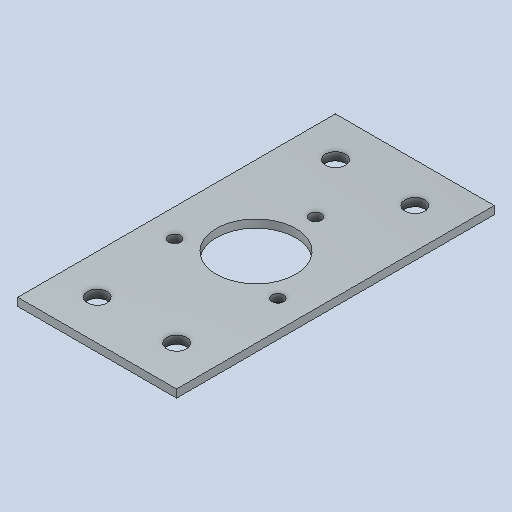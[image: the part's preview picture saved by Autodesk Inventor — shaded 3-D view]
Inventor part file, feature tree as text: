
AUTODESK INVENTOR PART (.ipt)
format: ipt  version: 2023 (Build 270158000, 158)  size: 137,216 bytes
history: native  units: mm
features: other x1, extrude x1, sketch x1
ambient origin geometry x8: Origin, YZ Plane, XZ Plane, XY Plane, X Axis, Y Axis, Z Axis, Center Point
bodies: Body1 (feature_tree)
feature tree (3):
  other  "Sólido1"
  extrude  "Extrusão1"  Depth=80.0mm
  sketch  "Esboço1"  dims[d0=40.0mm d1=80.0mm d2=2.0mm d3=0.0mm d19=40.0mm d20=10.0mm d21=10.0mm d60=5.0mm d61=10.0mm d63=20.0mm d64=10.0mm d65=10.0mm d66=20.0mm d67=20.0mm d68=3.0mm d69=15.0mm d70=30.0mm d72=360.0deg]
